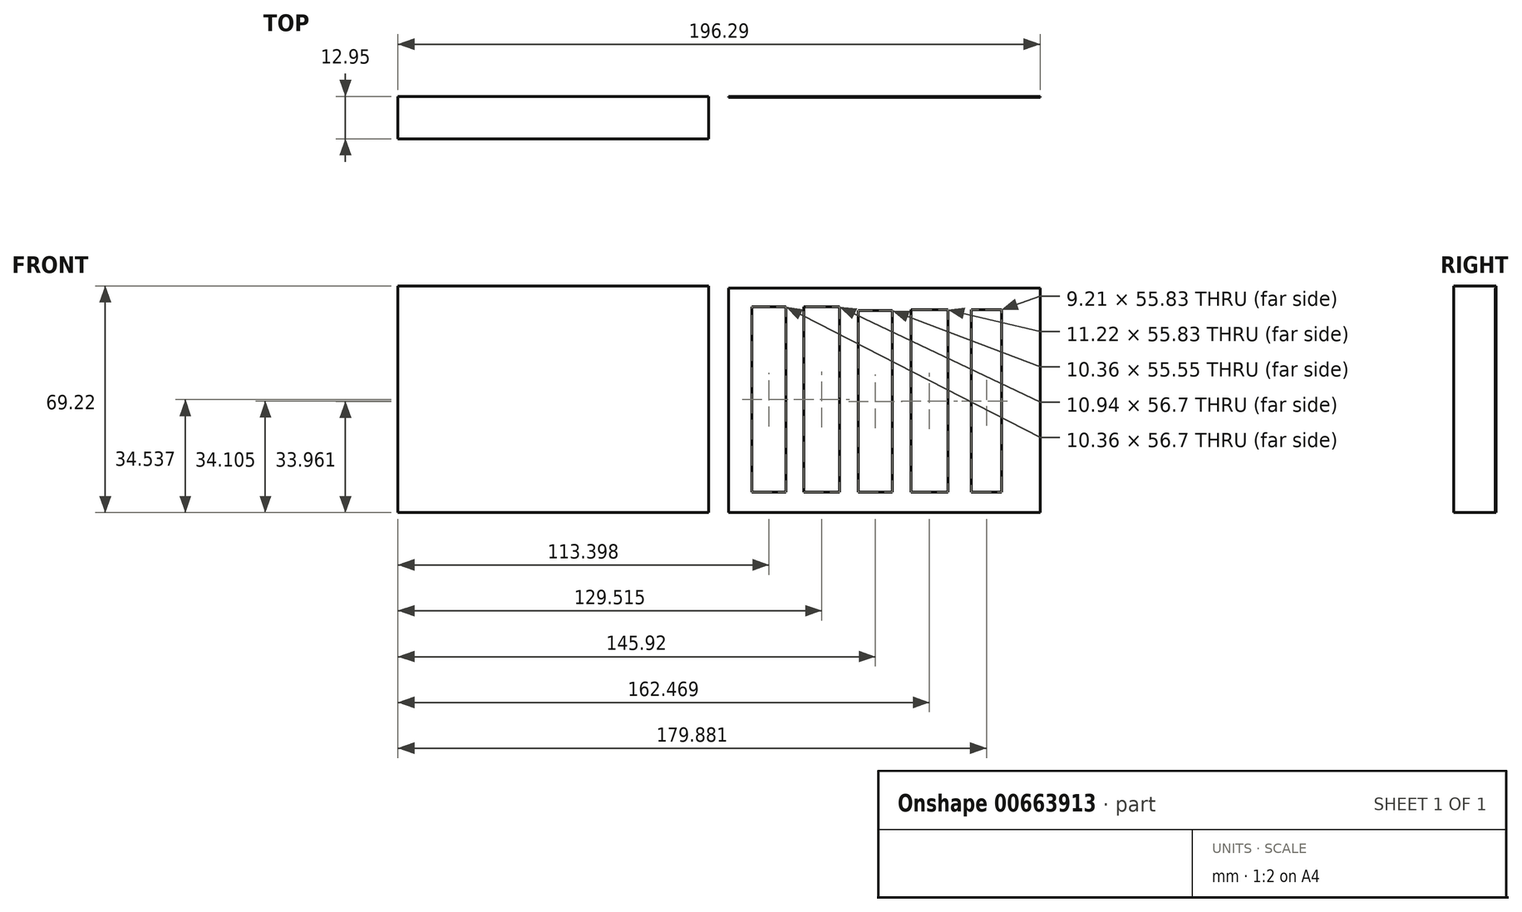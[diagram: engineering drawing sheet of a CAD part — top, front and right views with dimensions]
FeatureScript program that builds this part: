
annotation { "Feature Type Name" : "Feature", "Feature Type Description" : "" }
export const myFeature = defineFeature(function(context is Context, id is Id, definition is map)
    precondition{}
    {
        {
            var Q0;
            Q0=qCreatedBy(makeId("Front.planeOp"),FACE);
            var sketch = newSketch(context, id + "F0", { "sketchPlane" : qUnion([Q0])});
            skLineSegment(sketch, "E0.bottom", {"start": v(-98, 69.22) * mm, "end": v(-3.02, 69.22) * mm});
            skLineSegment(sketch, "E0.top", {"start": v(-98, 0) * mm, "end": v(-3.02, 0) * mm});
            skLineSegment(sketch, "E0.left", {"start": v(-98, 69.22) * mm, "end": v(-98, 0) * mm});
            skLineSegment(sketch, "E0.right", {"start": v(-3.02, 69.22) * mm, "end": v(-3.02, 0) * mm});
            skSolve(sketch);
        }
        {
            var Q0;
            Q0 = qSketchRegion(id + "F0", true);
            extrude(context, id + "F1", {"entities" : qUnion([Q0]), "depth" : 0.25 * mm, "offsetDistance" : 25.4 * mm});
        }
        {
            var Q0;
            Q0=qCreatedBy(makeId("Front.planeOp"),FACE);
            var sketch = newSketch(context, id + "F2", { "sketchPlane" : qUnion([Q0])});
            skLineSegment(sketch, "E1.bottom", {"start": v(3.02, 68.64) * mm, "end": v(98.29, 68.64) * mm});
            skLineSegment(sketch, "E1.top", {"start": v(3.02, 0) * mm, "end": v(98.29, 0) * mm});
            skLineSegment(sketch, "E1.left", {"start": v(3.02, 68.64) * mm, "end": v(3.02, 0) * mm});
            skLineSegment(sketch, "E1.right", {"start": v(98.29, 68.64) * mm, "end": v(98.29, 0) * mm});
            skLineSegment(sketch, "E2.bottom", {"start": v(10.22, 62.89) * mm, "end": v(20.58, 62.89) * mm});
            skLineSegment(sketch, "E2.top", {"start": v(10.22, 6.19) * mm, "end": v(20.58, 6.19) * mm});
            skLineSegment(sketch, "E2.left", {"start": v(10.22, 62.89) * mm, "end": v(10.22, 6.19) * mm});
            skLineSegment(sketch, "E2.right", {"start": v(20.58, 62.89) * mm, "end": v(20.58, 6.19) * mm});
            skLineSegment(sketch, "E3.bottom", {"start": v(26.05, 62.89) * mm, "end": v(36.98, 62.89) * mm});
            skLineSegment(sketch, "E3.top", {"start": v(26.05, 6.19) * mm, "end": v(36.98, 6.19) * mm});
            skLineSegment(sketch, "E3.left", {"start": v(26.05, 62.89) * mm, "end": v(26.05, 6.19) * mm});
            skLineSegment(sketch, "E3.right", {"start": v(36.98, 62.89) * mm, "end": v(36.98, 6.19) * mm});
            skLineSegment(sketch, "E4.bottom", {"start": v(42.74, 61.73) * mm, "end": v(53.1, 61.73) * mm});
            skLineSegment(sketch, "E4.top", {"start": v(42.74, 6.19) * mm, "end": v(53.1, 6.19) * mm});
            skLineSegment(sketch, "E4.left", {"start": v(42.74, 61.73) * mm, "end": v(42.74, 6.19) * mm});
            skLineSegment(sketch, "E4.right", {"start": v(53.1, 61.73) * mm, "end": v(53.1, 6.19) * mm});
            skLineSegment(sketch, "E5.bottom", {"start": v(58.86, 62.02) * mm, "end": v(70.08, 62.02) * mm});
            skLineSegment(sketch, "E5.top", {"start": v(58.86, 6.19) * mm, "end": v(70.08, 6.19) * mm});
            skLineSegment(sketch, "E5.left", {"start": v(58.86, 62.02) * mm, "end": v(58.86, 6.19) * mm});
            skLineSegment(sketch, "E5.right", {"start": v(70.08, 62.02) * mm, "end": v(70.08, 6.19) * mm});
            skLineSegment(sketch, "E6.bottom", {"start": v(77.28, 62.02) * mm, "end": v(86.49, 62.02) * mm});
            skLineSegment(sketch, "E6.top", {"start": v(77.28, 6.19) * mm, "end": v(86.49, 6.19) * mm});
            skLineSegment(sketch, "E6.left", {"start": v(77.28, 62.02) * mm, "end": v(77.28, 6.19) * mm});
            skLineSegment(sketch, "E6.right", {"start": v(86.49, 62.02) * mm, "end": v(86.49, 6.19) * mm});
            skSolve(sketch);
        }
        {
            var Q0;
            Q0 = qSketchRegion(id + "F2", true);
            extrude(context, id + "F3", {"entities" : qUnion([Q0]), "depth" : 0.25 * mm, "offsetDistance" : 25.4 * mm});
        }
        {
            var Q0;
            Q0=makeQuery(id+"F1.opExtrude","CAP_FACE",FACE,{"disambiguationData":[OSD([sQuery(id+"F0.wireOp",EDGE,"E0.bottom"),sQuery(id+"F0.wireOp",EDGE,"E0.top"),sQuery(id+"F0.wireOp",EDGE,"E0.left"),sQuery(id+"F0.wireOp",EDGE,"E0.right")])],"isStart":false});
            extrude(context, id + "F4", {"entities" : qUnion([Q0]), "operationType" : NewBodyOperationType.ADD, "depth" : 12.7 * mm, "offsetDistance" : 25.4 * mm});
        }
    });
